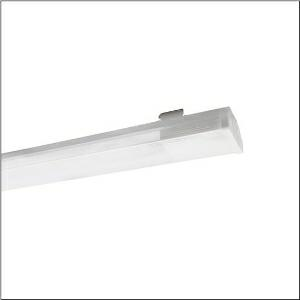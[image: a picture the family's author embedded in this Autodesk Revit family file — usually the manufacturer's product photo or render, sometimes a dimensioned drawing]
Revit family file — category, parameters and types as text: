
# Revit family: modario_r__31_gen_2_53bm812du4m1d2_0985
name_source: partatom
category: Lighting Fixtures
units: mm (PartAtom-declared; Revit-internal decimal feet)

## family parameters
Cut with Voids When Loaded = No
Host = Face
Light Source = No
Part Type = Normal
Room Calculation Point = No
Round Connector Dimension = Use Diameter
Shared = No

## types (1)
- --- (1 x LED, 26560 lm, 146.1 W, 4000K)
    Apparent Load = 146 VA
    CIE Flux Codes = 47 80 95 93 100
    Color Rendering = 80
    Color Temperature = 4000K
    Default Elevation = 1800 mm
    Description = Modario® 31 Gen.2, luminaire insert, of sheet steel, coil coated, white, length: 2.392mm, width: 81mm, height: 82mm, 8x system unit, system units: 299mm, LED rated luminous flux: 26.560lm, light colour: 840, control gear: DALI 2, control gear: ECG DALI, with plug, 5-pole, with phase selection, mains connection: 220..240V, AC, 50/60Hz, rated input power: 146W, through-wiring accessed according to module size, primary optical cover: cover, of PMMA, light emission: direct distribution, primary light characteristic: symmetric, protection rating (complete): IP20, protection rating (LED compartment): IP50, insulation class (complete): insulation class I (protective earthing), certification: CE, ENEC, VDE, UKCA, impact resistance: IK03, permissible ambient temperature for indoor applications: -40..+30°C, corresponds to IFS (International Featured Standards) requirements for safety and quality in the food industry, reducing of maximum allowable ambient temperature of 5°C with ceiling mounting, packaging unit: 1 piece
    Height = 92 mm
    Lamp = 1 x LED
    Lamp Light Flux = 26560 lm
    Lamp Power = 146.1 W
    Lamp count = 1
    Length = 2392 mm
    Luminous efficacy = 182 lm/W
    Manufacturer = Siteco
    ModVariant = No
    Model = 53BM812DU4M1D2
    Mounting Place = Ceiling
    Mounting Type = Pendant
    Number of Poles = 1
    OnlyDefault = Yes
    Power Factor = 1
    Product Name = Modario® 31 Gen.2
    Product group = luminaire insert | ceiling pendant
    ProductGroupID = 902
    Protection Class = Protection class I
    Protection Degree = IP 20
    RLX_Detail_Level = 1
    RLX_Emergency_Light_Flux = 0 lm
    RLX_Emergency_Type = 0
    RLX_Emergency_Type_DB = No
    RlxData = <blob elided: 37849 chars, md5=4d32744b>
    Socket = socket
    Standby Power = 0 W
    System Light Flux = 26560 lm
    System Power = 146 W
    Type Comments = factory setting: luminous flux: 100 % | dim-lin: 254 | 676 mA
    Type Image = l_1341883.jpg
    URL = http://relux.com
    VarID = @adj_064335
    Voltage = 0 V
    Weight = 0.00 kg
    Width = 81 mm

## geometry (parser evidence)
native form markers: Blend x4, Sweep x11
no freeform markers — native parametric forms only
